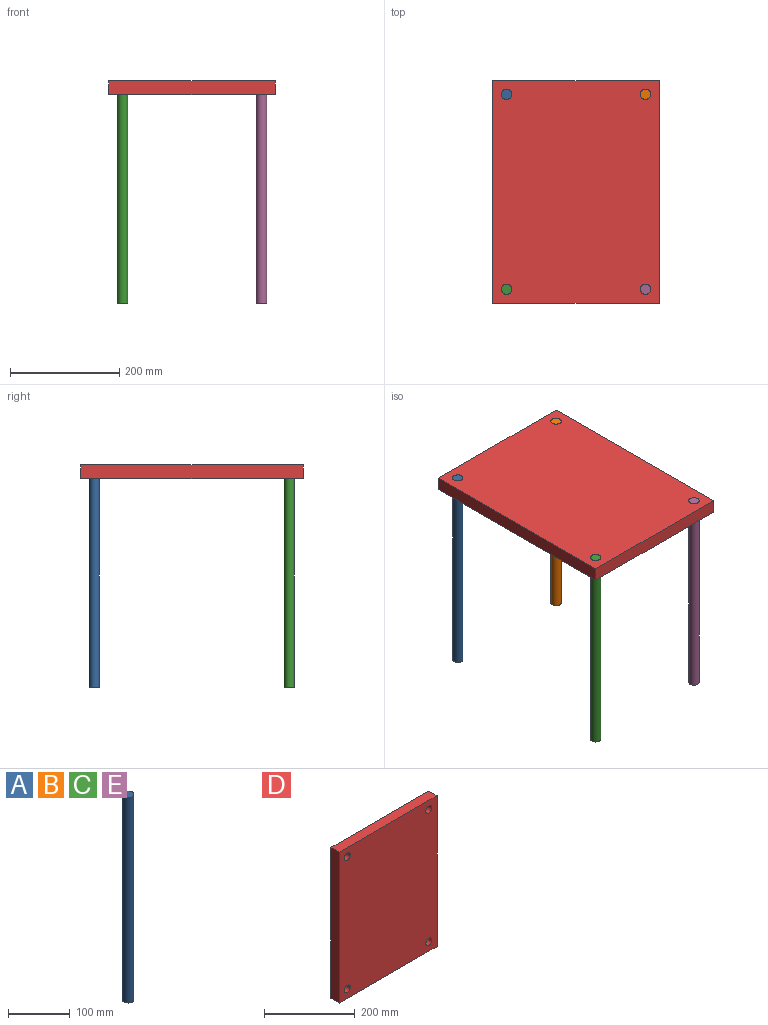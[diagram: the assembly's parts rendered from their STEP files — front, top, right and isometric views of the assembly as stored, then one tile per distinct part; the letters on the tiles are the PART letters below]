
ASSEMBLY  parts=5 mates=4
PART A: 3 faces, bbox 19.1x19.1x406.4 mm
  f0: cylinder r=9.53mm len=406.4mm, axis (0,0,-1), area 24322mm2, adj f1,f2
  f1: plane 19.05x19.05mm, normal (0,0,1), area 285mm2, adj f0
  f2: plane 19.05x19.05mm, normal (0,0,-1), area 285mm2, adj f0
PART B: same geometry as A
PART C: same geometry as A
PART D: 10 faces, bbox 304.8x25.4x406.4 mm
  f0: plane 304.8x25.4mm, normal (0,0,1), area 7741.9mm2, adj f1,f3,f4,f5
  f1: plane 406.4x25.4mm, normal (-1,0,0), area 10322.6mm2, adj f0,f2,f4,f5
  f2: plane 304.8x25.4mm, normal (0,0,-1), area 7741.9mm2, adj f1,f3,f4,f5
  f3: plane 406.4x25.4mm, normal (1,0,0), area 10322.6mm2, adj f0,f2,f4,f5
  f4: plane 406.4x304.8mm, normal (0,-1,0), area 122730.6mm2, adj f0,f1,f2,f3,f6,f7,f8,f9
  f5: plane 406.4x304.8mm, normal (0,1,0), area 122730.6mm2, adj f0,f1,f2,f3,f6,f7,f8,f9
  f6: cylinder r=9.53mm len=25.4mm, axis (0,-1,0), area 1520.1mm2, adj f4,f5
  f7: cylinder r=9.53mm len=25.4mm, axis (0,-1,0), area 1520.1mm2, adj f4,f5
  f8: cylinder r=9.53mm len=25.4mm, axis (0,-1,0), area 1520.1mm2, adj f4,f5
  f9: cylinder r=9.53mm len=25.4mm, axis (0,-1,0), area 1520.1mm2, adj f4,f5
PART E: same geometry as A
PLACE A t=(-351.48,-8.71,-131.85)mm
PLACE B t=(-97.48,-8.71,-131.85)mm
PLACE C t=(-351.48,-365.16,-131.85)mm
PLACE D rot(axis=(-1,0,0),90deg) t=(-165.57,-186.94,249.15)mm
PLACE E t=(-97.48,-365.16,-131.85)mm
MATE parallel D.f7 <-> B.f0  axis (0,0,1) through (-97.48,-8.71,274.55)mm
MATE parallel C.f0 <-> D.f9  axis (0,0,1) through (-351.48,-365.16,274.55)mm
MATE parallel A.f0 <-> D.f6  axis (0,0,1) through (-351.48,-8.71,274.55)mm
MATE parallel E.f0 <-> D.f8  axis (0,0,1) through (-97.48,-365.16,274.55)mm
